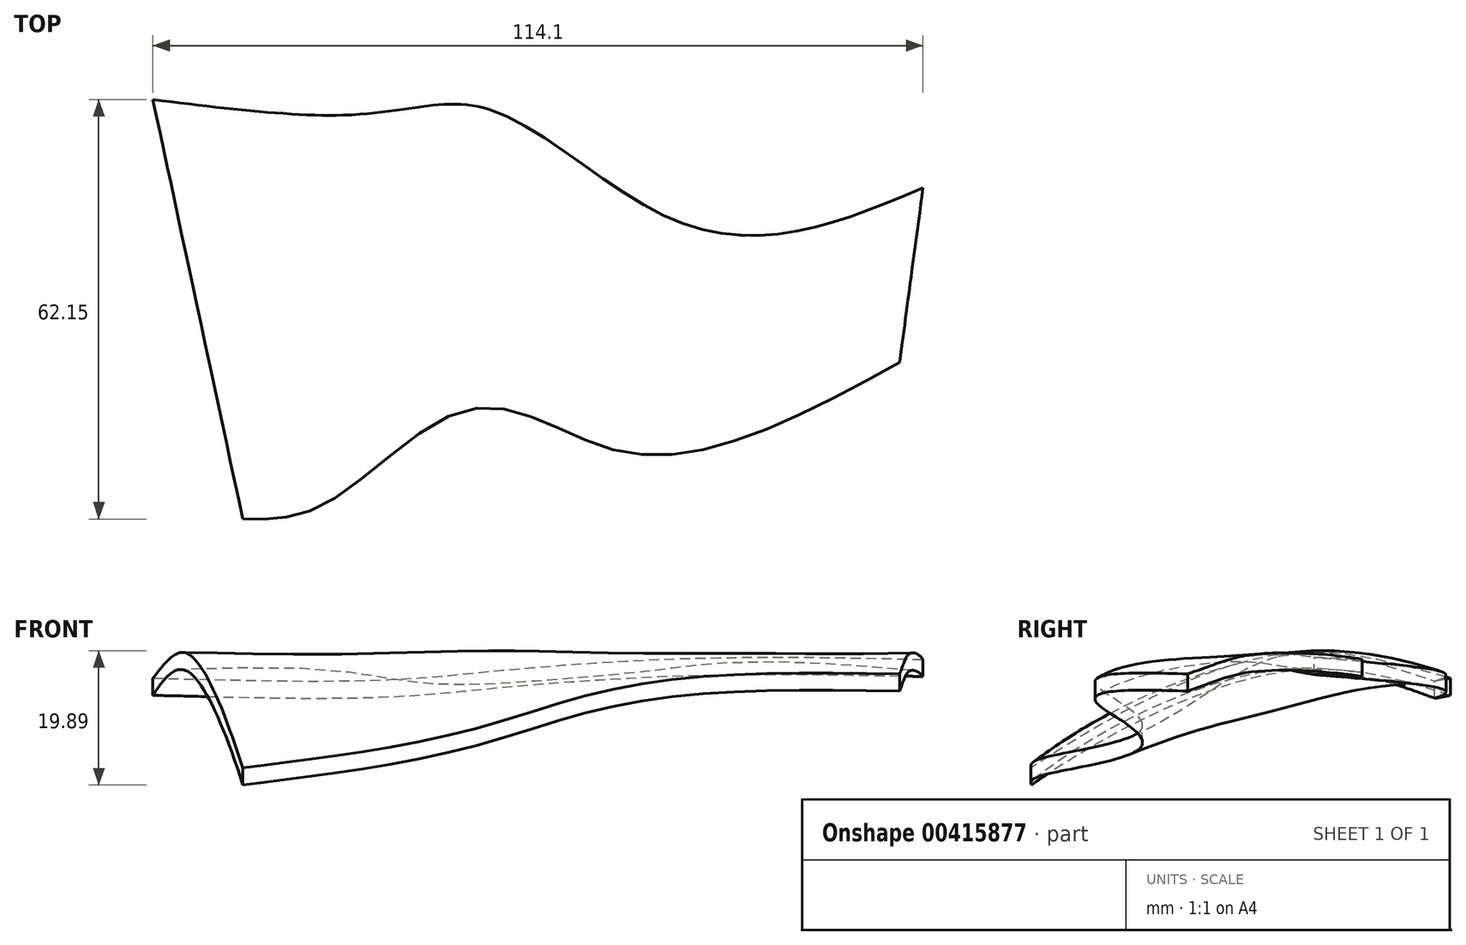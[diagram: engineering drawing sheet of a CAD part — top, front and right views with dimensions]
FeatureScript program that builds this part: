
annotation { "Feature Type Name" : "Feature", "Feature Type Description" : "" }
export const myFeature = defineFeature(function(context is Context, id is Id, definition is map)
    precondition{}
    {
        {
            var Q0;
            Q0=qCreatedBy(makeId("Top.planeOp"),FACE);
            var sketch = newSketch(context, id + "F0", { "sketchPlane" : qUnion([Q0])});
            skFitSpline(sketch, "E0", {"points": [v(0, 0) * mm, v(22.05, 0.96) * mm, v(42.45, 0) * mm, v(68.03, -3.75) * mm, v(93.7, -6.8) * mm, v(106.55, -4.92) * mm, v(109.13, -6.13) * mm], "startDerivative": vector(123.09, 26.38) * mm, "endDerivative": vector(61.74, -22.72) * mm});
            skSolve(sketch);
        }
        {
            var Q0;
            Q0=sQuery(id+"F0.wireOp",VERTEX,"E0.start");
            var Q1;
            Q1=sQuery(id+"F0.wireOp",EDGE,"E0");
            cPlane(context, id + "F1", {"entities" : qUnion([Q0, Q1]), "cplaneType" : CPlaneType.CURVE_POINT, "offset" : 25.4 * mm, "width" : 152.4 * mm, "height" : 152.4 * mm});
        }
        {
            var Q0;
            Q0=qCreatedBy(id+"F1.planeOp",FACE);
            var sketch = newSketch(context, id + "F2", { "sketchPlane" : qUnion([Q0])});
            skFitSpline(sketch, "E1", {"points": [v(25.4, -3.42) * mm, v(-0.9, 0) * mm, v(-38.1, -16.71) * mm], "startDerivative": vector(-61.42, 16.2) * mm, "endDerivative": vector(-64.3, -41.93) * mm});
            skFitSpline(sketch, "E2", {"points": [v(25.4, -5.96) * mm, v(0, -2.54) * mm, v(-38.1, -19.25) * mm], "startDerivative": vector(-59.13, 18.6) * mm, "endDerivative": vector(-64.9, -43.8) * mm});
            skLineSegment(sketch, "E3", {"start": v(25.4, -3.42) * mm, "end": v(25.4, -5.96) * mm});
            skLineSegment(sketch, "E4", {"start": v(-38.1, -16.71) * mm, "end": v(-38.1, -19.25) * mm});
            skSolve(sketch);
        }
        {
            var Q0;
            Q0=sQuery(id+"F0.wireOp",VERTEX,"E0.1.internal");
            var Q1;
            Q1=sQuery(id+"F0.wireOp",EDGE,"E0");
            cPlane(context, id + "F3", {"entities" : qUnion([Q0, Q1]), "cplaneType" : CPlaneType.CURVE_POINT, "offset" : 25.4 * mm, "width" : 152.4 * mm, "height" : 152.4 * mm});
        }
        {
            var Q0;
            Q0=qCreatedBy(id+"F3.planeOp",FACE);
            var sketch = newSketch(context, id + "F4", { "sketchPlane" : qUnion([Q0])});
            skPoint(sketch, "E5.0", {"position": v(1.8, 0) * mm});
            skFitSpline(sketch, "E6", {"points": [v(23.38, -6.39) * mm, v(1.8, -2.54) * mm, v(-33.97, -17.6) * mm], "startDerivative": vector(-50.7, 19.08) * mm, "endDerivative": vector(-59.42, -45.11) * mm});
            skFitSpline(sketch, "E7", {"points": [v(23.38, -3.85) * mm, v(1.8, 0) * mm, v(-33.97, -15.06) * mm], "startDerivative": vector(-50.79, 17.94) * mm, "endDerivative": vector(-59.96, -44.79) * mm});
            skLineSegment(sketch, "E8", {"start": v(23.38, -3.85) * mm, "end": v(23.38, -6.39) * mm});
            skLineSegment(sketch, "E9", {"start": v(-33.97, -15.06) * mm, "end": v(-33.97, -17.6) * mm});
            skSolve(sketch);
        }
        {
            var Q0;
            Q0=sQuery(id+"F0.wireOp",VERTEX,"E0.2.internal");
            var Q1;
            Q1=sQuery(id+"F0.wireOp",EDGE,"E0");
            cPlane(context, id + "F5", {"entities" : qUnion([Q0, Q1]), "cplaneType" : CPlaneType.CURVE_POINT, "offset" : 25.4 * mm, "width" : 152.4 * mm, "height" : 152.4 * mm});
        }
        {
            var Q0;
            Q0=qCreatedBy(id+"F5.planeOp",FACE);
            var sketch = newSketch(context, id + "F6", { "sketchPlane" : qUnion([Q0])});
            skFitSpline(sketch, "E10", {"points": [v(27.18, -2.43) * mm, v(3.68, 0) * mm, v(-17.69, -11.4) * mm], "startDerivative": vector(-35.42, 12.22) * mm, "endDerivative": vector(-53.86, -23.61) * mm});
            skFitSpline(sketch, "E11", {"points": [v(27.18, -4.97) * mm, v(3.68, -7.88) * mm, v(-17.69, -13.93) * mm], "startDerivative": vector(-35.46, 11.6) * mm, "endDerivative": vector(-55.33, -19.57) * mm});
            skLineSegment(sketch, "E12", {"start": v(27.18, -2.43) * mm, "end": v(27.18, -4.97) * mm});
            skLineSegment(sketch, "E13", {"start": v(-17.69, -11.4) * mm, "end": v(-17.69, -13.93) * mm});
            skSolve(sketch);
        }
        {
            var Q0;
            Q0=sQuery(id+"F0.wireOp",VERTEX,"E0.3.internal");
            var Q1;
            Q1=sQuery(id+"F0.wireOp",EDGE,"E0");
            cPlane(context, id + "F7", {"entities" : qUnion([Q0, Q1]), "cplaneType" : CPlaneType.CURVE_POINT, "offset" : 25.4 * mm, "width" : 152.4 * mm, "height" : 152.4 * mm});
        }
        {
            var Q0;
            Q0=qCreatedBy(id+"F7.planeOp",FACE);
            var sketch = newSketch(context, id + "F8", { "sketchPlane" : qUnion([Q0])});
            skPoint(sketch, "E14.0", {"position": v(9.03, 0) * mm});
            skFitSpline(sketch, "E15", {"points": [v(20.74, -0.63) * mm, v(9.03, 0) * mm, v(-14.85, -4.92) * mm], "startDerivative": vector(-41.07, 8.1) * mm, "endDerivative": vector(-29.76, -16.98) * mm});
            skFitSpline(sketch, "E16", {"points": [v(20.65, -3.17) * mm, v(9.03, -2.54) * mm, v(-14.85, -7.46) * mm], "startDerivative": vector(-40.96, 7.35) * mm, "endDerivative": vector(-29.79, -16.48) * mm});
            skLineSegment(sketch, "E17", {"start": v(20.74, -0.63) * mm, "end": v(20.65, -3.17) * mm});
            skLineSegment(sketch, "E18", {"start": v(-14.85, -4.92) * mm, "end": v(-14.85, -7.46) * mm});
            skSolve(sketch);
        }
        {
            var Q0;
            Q0=sQuery(id+"F0.wireOp",VERTEX,"E0.5.internal");
            var Q1;
            Q1=sQuery(id+"F0.wireOp",EDGE,"E0");
            cPlane(context, id + "F9", {"entities" : qUnion([Q0, Q1]), "cplaneType" : CPlaneType.CURVE_POINT, "offset" : 25.4 * mm, "width" : 152.4 * mm, "height" : 152.4 * mm});
        }
        {
            var Q0;
            Q0=qCreatedBy(id+"F9.planeOp",FACE);
            var sketch = newSketch(context, id + "F10", { "sketchPlane" : qUnion([Q0])});
            skPoint(sketch, "E19.0", {"position": v(9.26, 0) * mm});
            skFitSpline(sketch, "E20", {"points": [v(26.1, -0.64) * mm, v(9.26, 0) * mm, v(0, -2.8) * mm], "startDerivative": vector(-26.56, 4.76) * mm, "endDerivative": vector(-25.93, -8.2) * mm});
            skFitSpline(sketch, "E21", {"points": [v(26.1, -3.18) * mm, v(9.26, -2.54) * mm, v(0, -5.34) * mm], "startDerivative": vector(-26.1, 4.1) * mm, "endDerivative": vector(-25.82, -8.38) * mm});
            skLineSegment(sketch, "E22", {"start": v(26.1, -0.64) * mm, "end": v(26.1, -3.18) * mm});
            skLineSegment(sketch, "E23", {"start": v(0, -2.8) * mm, "end": v(0, -5.34) * mm});
            skSolve(sketch);
        }
        {
            var Q0;
            Q0=makeQuery(id+"F2.imprint","IMPRINT",FACE,{"disambiguationData":[TD([[makeQuery(id+"F2.imprint","IMPRINT",EDGE,{"derivedFrom":sQuery(id+"F2.wireOp",EDGE,"E1")}),1.0]])]});
            var Q1;
            Q1=makeQuery(id+"F4.imprint","IMPRINT",FACE,{"disambiguationData":[TD([[makeQuery(id+"F4.imprint","IMPRINT",EDGE,{"derivedFrom":sQuery(id+"F4.wireOp",EDGE,"E6")}),-1.0]])]});
            var Q2;
            Q2=makeQuery(id+"F6.imprint","IMPRINT",FACE,{"disambiguationData":[TD([[makeQuery(id+"F6.imprint","IMPRINT",EDGE,{"derivedFrom":sQuery(id+"F6.wireOp",EDGE,"E10")}),1.0]])]});
            var Q3;
            Q3=makeQuery(id+"F8.imprint","IMPRINT",FACE,{"disambiguationData":[TD([[makeQuery(id+"F8.imprint","IMPRINT",EDGE,{"derivedFrom":sQuery(id+"F8.wireOp",EDGE,"E15")}),1.0]])]});
            var Q4;
            Q4=makeQuery(id+"F10.imprint","IMPRINT",FACE,{"disambiguationData":[TD([[makeQuery(id+"F10.imprint","IMPRINT",EDGE,{"derivedFrom":sQuery(id+"F10.wireOp",EDGE,"E20")}),1.0]])]});
            loft(context, id + "F11", {"sheetProfilesArray" : [{ "sheetProfileEntities" : qUnion([Q0]) }, { "sheetProfileEntities" : qUnion([Q1]) }, { "sheetProfileEntities" : qUnion([Q2]) }, { "sheetProfileEntities" : qUnion([Q3]) }, { "sheetProfileEntities" : qUnion([Q4]) }]});
        }
    });
